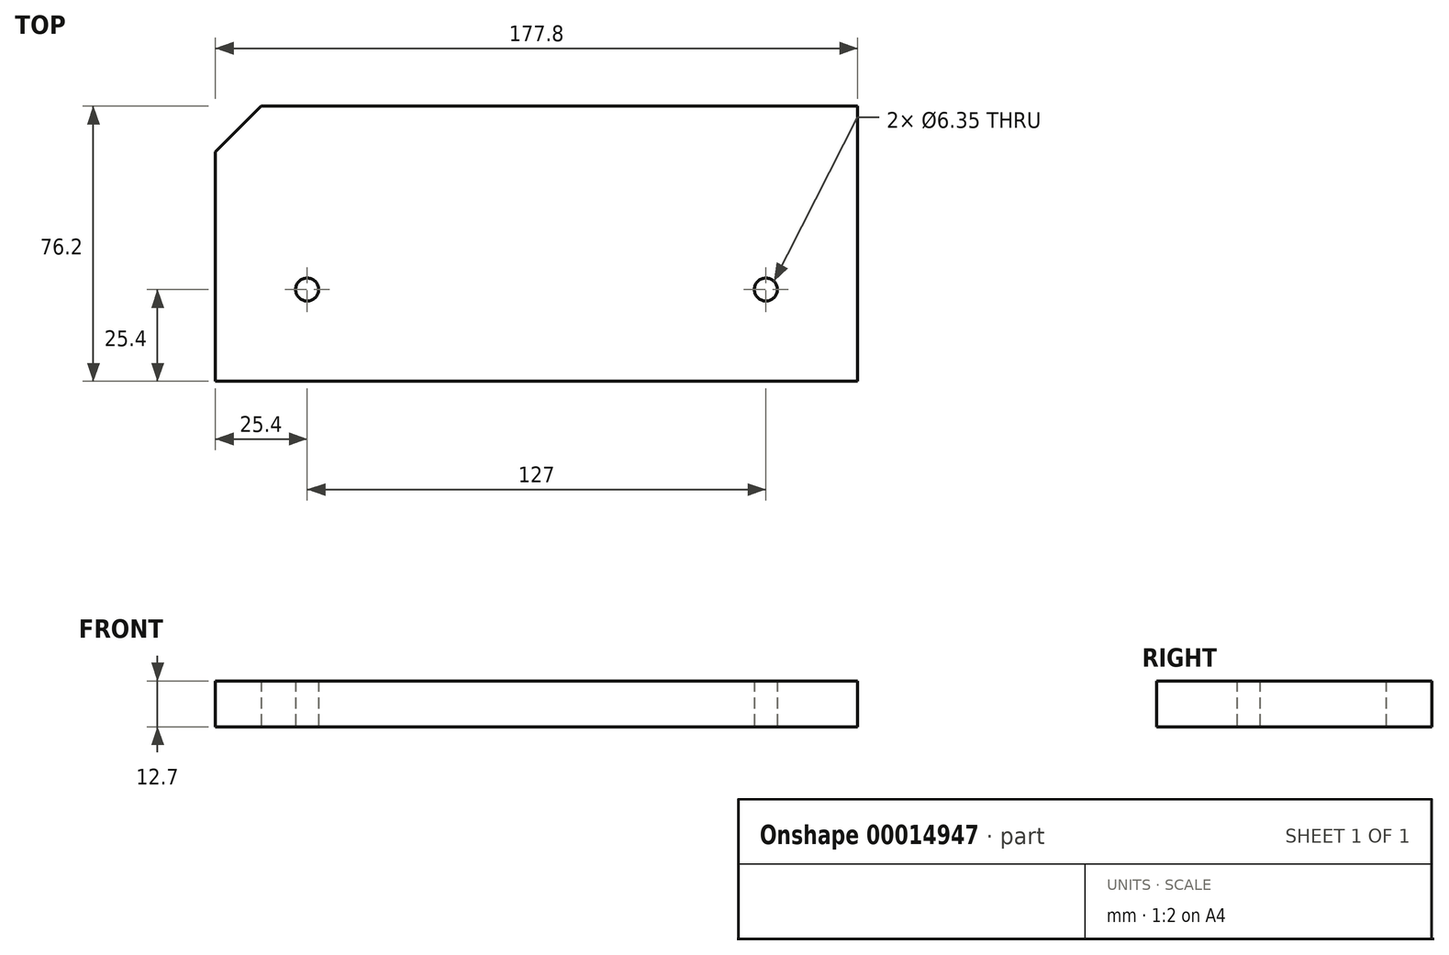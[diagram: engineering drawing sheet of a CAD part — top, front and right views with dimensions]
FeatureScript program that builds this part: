
annotation { "Feature Type Name" : "Feature", "Feature Type Description" : "" }
export const myFeature = defineFeature(function(context is Context, id is Id, definition is map)
    precondition{}
    {
        {
            var Q0;
            Q0=qCreatedBy(makeId("Top.planeOp"),FACE);
            var sketch = newSketch(context, id + "F0", { "sketchPlane" : qUnion([Q0])});
            skLineSegment(sketch, "E0.bottom", {"start": v(0, 0) * mm, "end": v(177.8, 0) * mm});
            skLineSegment(sketch, "E0.top", {"start": v(0, 76.2) * mm, "end": v(177.8, 76.2) * mm});
            skLineSegment(sketch, "E0.left", {"start": v(0, 0) * mm, "end": v(0, 76.2) * mm});
            skLineSegment(sketch, "E0.right", {"start": v(177.8, 0) * mm, "end": v(177.8, 76.2) * mm});
            skCircle(sketch, "E1", {"center": v(25.4, 25.4) * mm, "radius": 3.18 * mm});
            skCircle(sketch, "E2", {"center": v(152.4, 25.4) * mm, "radius": 3.18 * mm});
            skPoint(sketch, "E3", {"position": v(0, 63.5) * mm});
            skPoint(sketch, "E4", {"position": v(12.7, 76.2) * mm});
            skLineSegment(sketch, "E5", {"start": v(0, 63.5) * mm, "end": v(12.7, 76.2) * mm});
            skSolve(sketch);
        }
        {
            var Q0;
            Q0=makeQuery(id+"F0.imprint","IMPRINT",FACE,{"disambiguationData":[TD([[makeQuery(id+"F0.imprint","IMPRINT",EDGE,{"derivedFrom":sQuery(id+"F0.wireOp",EDGE,"E0.bottom")}),1.0]])]});
            extrude(context, id + "F1", {"entities" : qUnion([Q0]), "depth" : 12.7 * mm});
        }
    });
